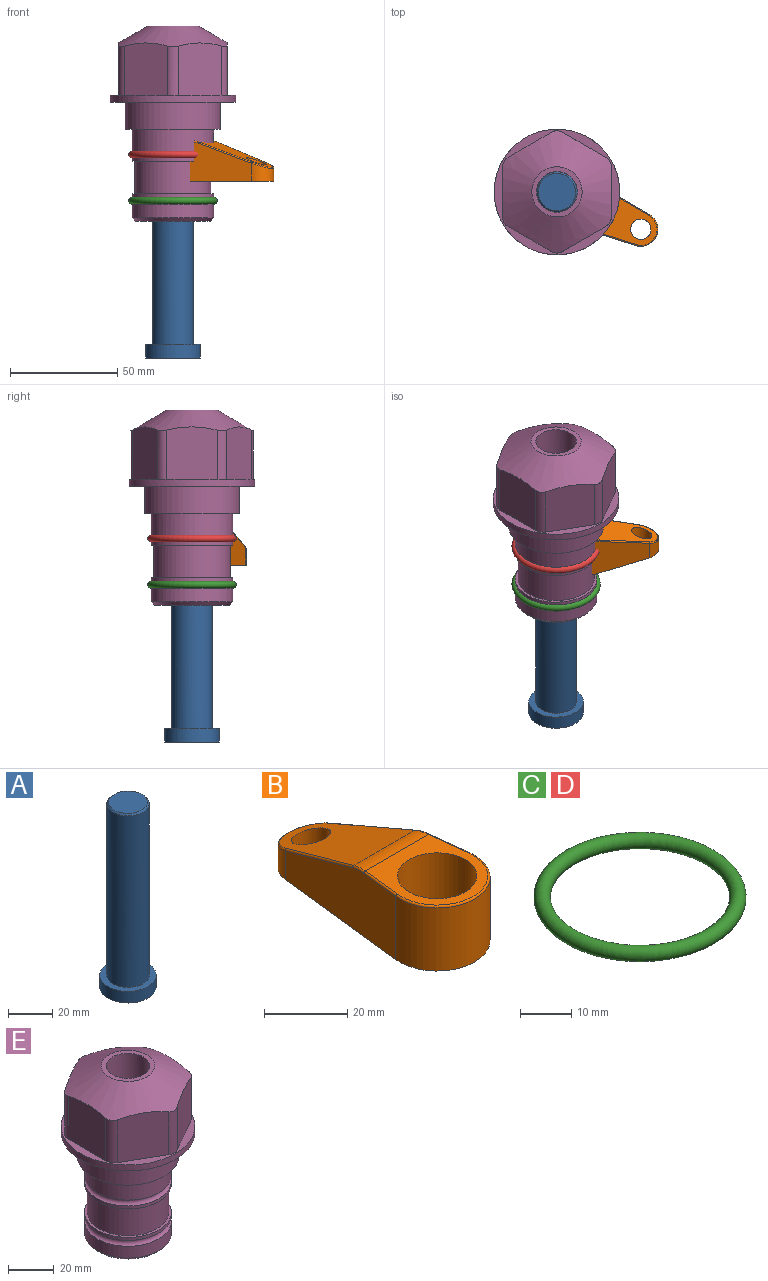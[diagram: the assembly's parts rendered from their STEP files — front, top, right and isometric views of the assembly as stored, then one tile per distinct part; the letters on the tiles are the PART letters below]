
ASSEMBLY  parts=5 mates=3
PART A: 6 faces, bbox 25.4x25.4x101.6 mm
  f0: plane 17.46x17.46mm, normal (0,0,1), area 239.5mm2, adj f5
  f1: plane 25.4x25.4mm, normal (0,0,-1), area 506.7mm2, adj f2
  f2: cylinder r=12.7mm len=25.4mm, axis (0,0,1), area 506.7mm2, adj f1,f3
  f3: plane 25.4x25.4mm, normal (0,0,1), area 221.7mm2, adj f2,f4
  f4: cylinder r=9.53mm len=94.46mm, axis (0,0,1), area 5653mm2, adj f3,f5
  f5: cone r=8.73mm half-angle=45deg, axis (0,0,-1), area 64.4mm2, adj f0,f4
PART B: 44 faces, bbox 27.5x64.5x19.1 mm
  f0: plane 2.3x0.95mm, normal (0,0,-1), area 1mm2, adj f25,f30,f34
  f1: plane 63.5x25.4mm, normal (0,0,-1), area 561.7mm2, adj f2,f3,f4,f5,f6,f7,f19,f20
  f2: cylinder r=12.7mm len=25.4mm, axis (0,0,-1), area 792.2mm2, adj f1,f3,f5,f13
  f3: plane 42.33x18.54mm, normal (0.99,0.11,0), area 647mm2, adj f1,f2,f4,f11,f12,f14
  f4: cylinder r=7.94mm len=15.78mm, axis (0,0,-1), area 158.6mm2, adj f1,f3,f5,f16
  f5: plane 42.33x18.54mm, normal (-0.99,0.11,0), area 647mm2, adj f1,f2,f4,f15,f17,f18
  f6: cylinder r=9.53mm len=19.05mm, axis (0,0,-1), area 1140.1mm2, adj f1,f8
  f7: cylinder r=4.76mm len=10.98mm, axis (0,0,-1), area 276.1mm2, adj f1,f9
  f8: plane 25.83x24.38mm, normal (0,0,1), area 262.2mm2, adj f6,f10,f11,f13,f15
  f9: plane 32.49x20.55mm, normal (0,0.34,0.94), area 489.9mm2, adj f7,f10,f14,f16,f18
  f10: cylinder r=12.7mm len=21.49mm, axis (-1,0,0), area 93.2mm2, adj f8,f9,f12,f17
  f11: cylinder r=0.51mm len=12.34mm, axis (0.11,-0.99,0), area 9.9mm2, adj f3,f8,f12,f13
  f12: bspline ~7.62x1.64mm, area 3.5mm2, adj f3,f10,f11,f14
  f13: torus R=12.19mm, axis (0,0,1), area 33.6mm2, adj f2,f8,f11,f15
  f14: cylinder r=0.51mm len=26.01mm, axis (0.1,-0.93,0.34), area 21.6mm2, adj f3,f9,f12,f16
  f15: cylinder r=0.51mm len=12.34mm, axis (0.11,0.99,0), area 9.9mm2, adj f5,f8,f13,f17
  f16: bspline ~15.78x7.05mm, area 15.7mm2, adj f4,f9,f14,f18
  f17: bspline ~7.62x1.64mm, area 3.5mm2, adj f5,f10,f15,f18
  f18: cylinder r=0.51mm len=26.01mm, axis (0.1,0.93,-0.34), area 21.6mm2, adj f5,f9,f16,f17
  f19: plane 21.6x14.29mm, normal (-0.99,-0.11,0), area 242.6mm2, adj f1,f26,f28,f34,f36,f38
  f20: plane 21.6x14.29mm, normal (0.99,-0.11,0), area 242.6mm2, adj f1,f27,f29,f37,f39,f41
  f21: cylinder r=12.7mm len=14.29mm, axis (0,0,-1), area 173.2mm2, adj f1,f26,f27,f30,f31,f33
  f22: cylinder r=7.94mm len=7.63mm, axis (0,0,-1), area 53.8mm2, adj f1,f28,f29,f42
  f23: plane 2.3x0.95mm, normal (0,0,-1), area 1mm2, adj f25,f33,f37
  f24: plane 17.94x12.32mm, normal (0,-0.34,-0.94), area 191.2mm2, adj f25,f38,f41,f42
  f25: cylinder r=9.53mm len=12.93mm, axis (-1,0,0), area 37.5mm2, adj f0,f23,f24,f31,f36,f39
  f26: cylinder r=1.59mm len=14.29mm, axis (0,0,-1), area 49mm2, adj f1,f19,f21,f32
  f27: cylinder r=1.59mm len=14.29mm, axis (0,0,-1), area 49mm2, adj f1,f20,f21,f35
  f28: cylinder r=1.59mm len=7.28mm, axis (0,0,-1), area 22.1mm2, adj f1,f19,f22,f40
  f29: cylinder r=1.59mm len=7.28mm, axis (0,0,-1), area 22.1mm2, adj f1,f20,f22,f43
  f30: torus R=14.29mm, axis (0,0,1), area 5.8mm2, adj f0,f21,f31,f32
  f31: bspline ~11.06x2.73mm, area 20.8mm2, adj f21,f25,f30,f33
  f32: sphere r=1.59mm, area 5.4mm2, adj f26,f30,f34
  f33: torus R=14.29mm, axis (0,0,1), area 5.8mm2, adj f21,f23,f31,f35
  f34: cylinder r=1.59mm len=1.68mm, axis (-0.11,0.99,0), area 2.4mm2, adj f0,f19,f32,f36
  f35: sphere r=1.59mm, area 5.4mm2, adj f27,f33,f37
  f36: bspline ~5.82x2.33mm, area 7.7mm2, adj f19,f25,f34,f38
  f37: cylinder r=1.59mm len=1.68mm, axis (0.11,0.99,0), area 2.4mm2, adj f20,f23,f35,f39
  f38: cylinder r=1.59mm len=18.33mm, axis (0.1,-0.93,0.34), area 46.7mm2, adj f19,f24,f36,f40
  f39: bspline ~5.82x2.33mm, area 7.7mm2, adj f20,f25,f37,f41
  f40: sphere r=1.59mm, area 3.6mm2, adj f28,f38,f42
  f41: cylinder r=1.59mm len=18.33mm, axis (0.1,0.93,-0.34), area 46.7mm2, adj f20,f24,f39,f43
  f42: bspline ~8.31x1.84mm, area 15.3mm2, adj f22,f24,f40,f43
  f43: sphere r=1.59mm, area 3.6mm2, adj f29,f41,f42
PART C: 1 faces, bbox 44.7x44.7x3.2 mm
  f0: torus R=19.05mm, axis (0,0,1), area 1193.9mm2
PART D: same geometry as C
PART E: 36 faces, bbox 58.7x58.7x91.2 mm
  f0: cylinder r=17.78mm len=35.56mm, axis (0,0,1), area 1670.8mm2, adj f23,f24,f31
  f1: cylinder r=19.05mm len=38.1mm, axis (0,0,1), area 1191.9mm2, adj f26,f27,f30
  f2: plane 58.66x58.66mm, normal (0,0,-1), area 1150.6mm2, adj f3,f28
  f3: cylinder r=29.33mm len=58.66mm, axis (0,0,-1), area 585.1mm2, adj f2,f4
  f4: plane 58.66x58.66mm, normal (0,0,1), area 475.9mm2, adj f3,f5,f6,f7,f8,f9,f10,f11
  f5: plane 24.5x20.32mm, normal (-0.5,0.87,0), area 562.8mm2, adj f4,f15,f16,f17
  f6: plane 24.5x20.32mm, normal (0.5,0.87,0), area 562.8mm2, adj f4,f14,f15,f17
  f7: plane 24.5x23.48mm, normal (1,0,0), area 562.8mm2, adj f4,f13,f14,f17
  f8: plane 24.5x20.32mm, normal (0.5,-0.87,0), area 562.8mm2, adj f4,f12,f13,f17
  f9: plane 24.5x20.32mm, normal (-0.5,-0.87,0), area 562.8mm2, adj f4,f11,f12,f17
  f10: plane 24.5x23.48mm, normal (-1,0,0), area 562.8mm2, adj f4,f11,f16,f17
  f11: cylinder r=5.08mm len=23.01mm, axis (0,0,-1), area 121.2mm2, adj f4,f9,f10,f17
  f12: cylinder r=5.08mm len=23.01mm, axis (0,0,-1), area 121.2mm2, adj f4,f8,f9,f17
  f13: cylinder r=5.08mm len=23.01mm, axis (0,0,-1), area 121.2mm2, adj f4,f7,f8,f17
  f14: cylinder r=5.08mm len=23.01mm, axis (0,0,-1), area 121.2mm2, adj f4,f6,f7,f17
  f15: cylinder r=5.08mm len=23.01mm, axis (0,0,-1), area 121.2mm2, adj f4,f5,f6,f17
  f16: cylinder r=5.08mm len=23.01mm, axis (0,0,-1), area 121.2mm2, adj f4,f5,f10,f17
  f17: cone r=11.73mm half-angle=60deg, axis (0,0,-1), area 2071.8mm2, adj f5,f6,f7,f8,f9,f10,f11,f12
  f18: plane 23.46x23.46mm, normal (0,0,1), area 147.4mm2, adj f17,f35
  f19: plane 34.93x34.93mm, normal (0,0,-1), area 958mm2, adj f29
  f20: cylinder r=19.05mm len=38.1mm, axis (0,0,1), area 760.1mm2, adj f21,f29
  f21: torus R=19.05mm, axis (0,0,1), area 565.3mm2, adj f20,f22
  f22: cylinder r=19.05mm len=38.1mm, axis (0,0,1), area 190mm2, adj f21,f23
  f23: plane 38.1x38.1mm, normal (0,0,1), area 146.9mm2, adj f0,f22
  f24: plane 38.1x38.1mm, normal (0,0,-1), area 146.9mm2, adj f0,f25
  f25: cylinder r=19.05mm len=38.1mm, axis (0,0,1), area 190mm2, adj f24,f26
  f26: torus R=19.05mm, axis (0,0,1), area 565.3mm2, adj f1,f25
  f27: plane 44.45x44.45mm, normal (0,0,-1), area 411.7mm2, adj f1,f28
  f28: cylinder r=22.23mm len=44.45mm, axis (0,0,1), area 1773.5mm2, adj f2,f27
  f29: cone r=19.05mm half-angle=45deg, axis (0,0,1), area 257.5mm2, adj f19,f20
  f30: cylinder r=3.17mm len=6.75mm, axis (-1,0,0), area 128mm2, adj f1,f33
  f31: cylinder r=3.17mm len=6.35mm, axis (-1,0,0), area 102.5mm2, adj f0,f33
  f32: plane 25.4x25.4mm, normal (0,0,1), area 506.7mm2, adj f33
  f33: cylinder r=12.7mm len=66.42mm, axis (0,0,-1), area 5236.2mm2, adj f30,f31,f32,f34
  f34: cone r=9.53mm half-angle=30deg, axis (0,0,-1), area 443.4mm2, adj f33,f35
  f35: cylinder r=9.53mm len=19.05mm, axis (0,0,-1), area 849mm2, adj f18,f34
PLACE A rot(axis=(0,0,-1),23.9deg) t=(0,0,-91.61)mm
PLACE B rot(axis=(0,0,-1),113.9deg) t=(0,0,-37)mm
PLACE C t=(0,0,-21.59)mm
PLACE D at identity
PLACE E at identity fixed
MATE fastened C.f0 <-> E.f0  axis (0,0,1) through (0,0,-46.1)mm
MATE cylindrical A.f2 <-> E.f0  axis (0,0,1) through (0,0,-65.97)mm
MATE fastened B.f2 <-> A.f2  axis (0,0,1) through (0,0,-17.95)mm
